# Revit family: PRD_FrankeWS_SnksSuprts_BracketForPlasterSinks_SIRX837
name_source: partatom
category: Plumbing Fixtures
revit_build: Autodesk Revit 2018 (Build: 20190510_1515(x64)
units: mm (PartAtom-declared; Revit-internal decimal feet)

## family parameters
Always vertical = No
Cut with Voids When Loaded = No
OmniClass Number = 23.40.20.21
OmniClass Title = Toilet and Bath Specialties
Part Type = Normal
Room Calculation Point = No
Round Connector Dimension = Use Diameter
Shared = Yes
Work Plane-Based = No

## types (3) — shared parameters
AssetType = Fixed
BIMObjectName = PRD_AR_SinkSupports_BracketForPlasterSinks_SIRX837
BracketMaterial = PRD_AR_StainlessSteel_SatinFinished
Category = Pr_20_85_09_88, Sink supports
Color = Stainless steel
Description = Pair of brackets for plaster sink.
Dimensions = 40 x 180 x 557 mm
DurationUnit = year
Features = stainless steel
Finish = Satin finished
Form = Wall-mounted
GrossWeight = 1.79 kg
IfcExportAs = IfcBuildingElementProxy
IfcExportType = NOTDEFINED
Manufacturer = KWC Group AG
ManufacturerName = KWC Group AG
ManufacturerURL = www.kwc.com
Material = Stainless steel
MaterialCode = stainless steel
MaterialsBracketsBody = stainless steel
stainless steel
MaterialsBracketsFinishAndColour = Satin finished
MaterialsLegsBody = stainless steel
MaterialsLegsFinishAndColour = satin finished
Model = SIRX837
ModelNumber = 2000103337
ModelReference = SIRX837
NBSDescription = Supports for sinks
NBSReference = 45-35-70/347
Name = Bracket for plaster sinks, SIRX837
NetWeight = 1.70 kg
NominalHeight = 557 mm  [stored 1.82743 ft]
NominalLength = 40 mm  [stored 0.131234 ft]
NominalWidth = 180 mm  [stored 0.590551 ft]
ProductInformation = https://pim.kwc.com
URL = www.kwc.com
Uniclass2015Code = Pr_20_85_09_88
Uniclass2015Title = Sink supports
Uniclass2015Version = Products v1.7
Version = 1
WarrantyDurationUnit = year
zero-valued in all types: offset 1pce

## per-type parameters (varying)
| type | 2pcs left | 2pcs right | left | right |
| SIRX837 1 piece right | No | No | No | Yes |
| SIRX837 1 piece left | No | No | Yes | No |
| SIRX837 2 pieces | Yes | Yes | No | No |

note: [stored X ft] marks values corroborated as IEEE doubles in the binary element streams (Revit-internal decimal feet)

## geometry (parser evidence)
native form markers: Sweep x3
no freeform markers — native parametric forms only
